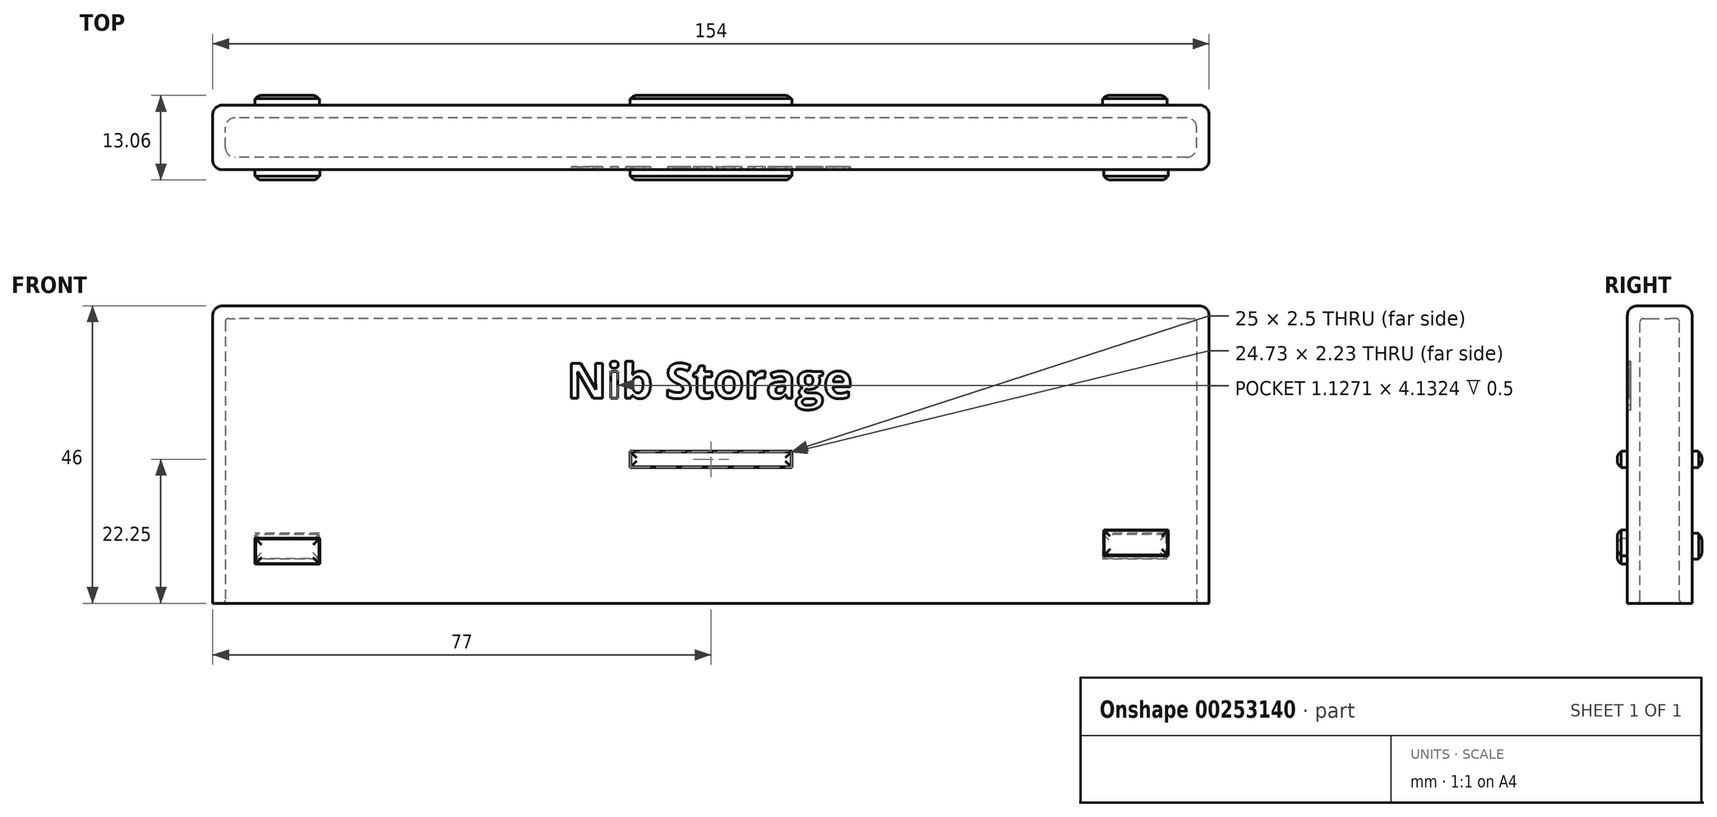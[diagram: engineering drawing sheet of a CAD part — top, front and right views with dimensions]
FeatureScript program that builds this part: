
annotation { "Feature Type Name" : "Feature", "Feature Type Description" : "" }
export const myFeature = defineFeature(function(context is Context, id is Id, definition is map)
    precondition{}
    {
        {
            var Q0;
            Q0=qCreatedBy(makeId("Top.planeOp"),FACE);
            var sketch = newSketch(context, id + "F0", { "sketchPlane" : qUnion([Q0])});
            skLineSegment(sketch, "E0.bottom", {"start": v(77, -5) * mm, "end": v(-77, -5) * mm});
            skLineSegment(sketch, "E0.top", {"start": v(77, 5) * mm, "end": v(-77, 5) * mm});
            skLineSegment(sketch, "E0.left", {"start": v(77, -5) * mm, "end": v(77, 5) * mm});
            skLineSegment(sketch, "E0.right", {"start": v(-77, -5) * mm, "end": v(-77, 5) * mm});
            skPoint(sketch, "E0.middle", {"position": v(0, 0) * mm});
            skSolve(sketch);
        }
        {
            var Q0;
            Q0 = qSketchRegion(id + "F0", true);
            extrude(context, id + "F1", {"entities" : qUnion([Q0]), "depth" : 46 * mm});
        }
        {
            var Q0;
            Q0=makeQuery(id+"F1.opExtrude","CAP_EDGE",EDGE,{"disambiguationData":[OSD([sQuery(id+"F0.wireOp",EDGE,"E0.top")])],"isStart":false});
            var Q1;
            Q1=makeQuery(id+"F1.opExtrude","CAP_EDGE",EDGE,{"disambiguationData":[OSD([sQuery(id+"F0.wireOp",EDGE,"E0.bottom")])],"isStart":false});
            var Q2;
            Q2=makeQuery(id+"F1.opExtrude","CAP_EDGE",EDGE,{"disambiguationData":[OSD([sQuery(id+"F0.wireOp",EDGE,"E0.right")])],"isStart":false});
            var Q3;
            Q3=makeQuery(id+"F1.opExtrude","CAP_EDGE",EDGE,{"disambiguationData":[OSD([sQuery(id+"F0.wireOp",EDGE,"E0.left")])],"isStart":false});
            var Q4;
            Q4=makeQuery(id+"F1.opExtrude","SWEPT_EDGE",EDGE,{"disambiguationData":[OSD([sQuery(id+"F0.wireOp",EDGE,"E0.top"),sQuery(id+"F0.wireOp",EDGE,"E0.right")])]});
            var Q5;
            Q5=makeQuery(id+"F1.opExtrude","SWEPT_EDGE",EDGE,{"disambiguationData":[OSD([sQuery(id+"F0.wireOp",EDGE,"E0.bottom"),sQuery(id+"F0.wireOp",EDGE,"E0.right")])]});
            var Q6;
            Q6=makeQuery(id+"F1.opExtrude","SWEPT_EDGE",EDGE,{"disambiguationData":[OSD([sQuery(id+"F0.wireOp",EDGE,"E0.top"),sQuery(id+"F0.wireOp",EDGE,"E0.left")])]});
            var Q7;
            Q7=makeQuery(id+"F1.opExtrude","SWEPT_EDGE",EDGE,{"disambiguationData":[OSD([sQuery(id+"F0.wireOp",EDGE,"E0.bottom"),sQuery(id+"F0.wireOp",EDGE,"E0.left")])]});
            fillet(context, id + "F2", {"entities" : qUnion([Q0, Q1, Q2, Q3, Q4, Q5, Q6, Q7]), "radius" : 1.5 * mm, "tangentPropagation" : true, "allowEdgeOverflow" : false});
        }
        {
            var Q0;
            Q0=makeQuery(id+"F1.opExtrude","CAP_FACE",FACE,{"disambiguationData":[OSD([sQuery(id+"F0.wireOp",EDGE,"E0.bottom"),sQuery(id+"F0.wireOp",EDGE,"E0.top"),sQuery(id+"F0.wireOp",EDGE,"E0.left"),sQuery(id+"F0.wireOp",EDGE,"E0.right")])],"isStart":true});
            shell(context, id + "F3", {"entities" : qUnion([Q0]), "thickness" : 1.95 * mm});
        }
        {
            var Q0;
            Q0=makeQuery(id+"F3.opShell","OFFSET_EDGE",EDGE,{"disambiguationData":[OSD([sQuery(id+"F0.wireOp",EDGE,"E0.top"),sQuery(id+"F0.wireOp",EDGE,"E0.left")])]});
            var Q1;
            Q1=makeQuery(id+"F3.opShell","OFFSET_EDGE",EDGE,{"disambiguationData":[OSD([sQuery(id+"F0.wireOp",EDGE,"E0.bottom"),sQuery(id+"F0.wireOp",EDGE,"E0.left")])]});
            var Q2;
            Q2=makeQuery(id+"F3.opShell","OFFSET_EDGE",EDGE,{"disambiguationData":[OSD([sQuery(id+"F0.wireOp",EDGE,"E0.bottom"),sQuery(id+"F0.wireOp",EDGE,"E0.right")])]});
            var Q3;
            Q3=makeQuery(id+"F3.opShell","OFFSET_EDGE",EDGE,{"disambiguationData":[OSD([sQuery(id+"F0.wireOp",EDGE,"E0.top"),sQuery(id+"F0.wireOp",EDGE,"E0.right")])]});
            fillet(context, id + "F4", {"entities" : qUnion([Q0, Q1, Q2, Q3]), "radius" : 1.5 * mm, "tangentPropagation" : true, "allowEdgeOverflow" : false});
        }
        {
            var Q0;
            Q0=makeQuery(id+"F1.opExtrude","SWEPT_FACE",FACE,{"disambiguationData":[OSD([sQuery(id+"F0.wireOp",EDGE,"E0.bottom")])]});
            var sketch = newSketch(context, id + "F5", { "sketchPlane" : qUnion([Q0])});
            skLineSegment(sketch, "E1", {"start": v(75.5, 22.25) * mm, "end": v(-75.5, 22.25) * mm, "construction": true});
            skLineSegment(sketch, "E2", {"start": v(0, 44.5) * mm, "end": v(0, 0) * mm, "construction": true});
            skLineSegment(sketch, "E3.bottom", {"start": v(-12.5, 23.5) * mm, "end": v(12.5, 23.5) * mm});
            skLineSegment(sketch, "E3.top", {"start": v(-12.5, 21) * mm, "end": v(12.5, 21) * mm});
            skLineSegment(sketch, "E3.left", {"start": v(-12.5, 23.5) * mm, "end": v(-12.5, 21) * mm});
            skLineSegment(sketch, "E3.right", {"start": v(12.5, 23.5) * mm, "end": v(12.5, 21) * mm});
            skPoint(sketch, "E3.middle", {"position": v(0, 22.25) * mm});
            skLineSegment(sketch, "E4", {"start": v(-75.5, 8.04) * mm, "end": v(75.5, 8.04) * mm, "construction": true});
            skLineSegment(sketch, "E5.bottom", {"start": v(-60.46, 6.04) * mm, "end": v(-70.46, 6.04) * mm});
            skLineSegment(sketch, "E5.top", {"start": v(-60.46, 10.04) * mm, "end": v(-70.46, 10.04) * mm});
            skLineSegment(sketch, "E5.left", {"start": v(-60.46, 6.04) * mm, "end": v(-60.46, 10.04) * mm});
            skLineSegment(sketch, "E5.right", {"start": v(-70.46, 6.04) * mm, "end": v(-70.46, 10.04) * mm});
            skPoint(sketch, "E5.middle", {"position": v(-65.46, 8.04) * mm});
            skLineSegment(sketch, "E6.bottom", {"start": v(60.69, 11.37) * mm, "end": v(70.69, 11.37) * mm});
            skLineSegment(sketch, "E6.top", {"start": v(60.69, 7.37) * mm, "end": v(70.69, 7.37) * mm});
            skLineSegment(sketch, "E6.left", {"start": v(60.69, 11.37) * mm, "end": v(60.69, 7.37) * mm});
            skLineSegment(sketch, "E6.right", {"start": v(70.69, 11.37) * mm, "end": v(70.69, 7.37) * mm});
            skPoint(sketch, "E6.middle", {"position": v(65.69, 9.37) * mm});
            skSolve(sketch);
        }
        {
            var Q0;
            Q0 = qSketchRegion(id + "F5", true);
            extrude(context, id + "F6", {"entities" : qUnion([Q0]), "operationType" : NewBodyOperationType.ADD, "depth" : 1.56 * mm});
        }
        {
            var Q0;
            Q0=makeQuery(id+"F6.opExtrude","CAP_EDGE",EDGE,{"disambiguationData":[OSD([sQuery(id+"F5.wireOp",EDGE,"E3.bottom")])],"isStart":false});
            var Q1;
            Q1=makeQuery(id+"F6.opExtrude","CAP_EDGE",EDGE,{"disambiguationData":[OSD([sQuery(id+"F5.wireOp",EDGE,"E3.right")])],"isStart":false});
            var Q2;
            Q2=makeQuery(id+"F6.opExtrude","CAP_EDGE",EDGE,{"disambiguationData":[OSD([sQuery(id+"F5.wireOp",EDGE,"E3.top")])],"isStart":false});
            var Q3;
            Q3=makeQuery(id+"F6.opExtrude","CAP_EDGE",EDGE,{"disambiguationData":[OSD([sQuery(id+"F5.wireOp",EDGE,"E3.left")])],"isStart":false});
            var Q4;
            Q4=makeQuery(id+"F6.opExtrude","CAP_EDGE",EDGE,{"disambiguationData":[OSD([sQuery(id+"F5.wireOp",EDGE,"E5.top")])],"isStart":false});
            var Q5;
            Q5=makeQuery(id+"F6.opExtrude","CAP_EDGE",EDGE,{"disambiguationData":[OSD([sQuery(id+"F5.wireOp",EDGE,"E5.left")])],"isStart":false});
            var Q6;
            Q6=makeQuery(id+"F6.opExtrude","CAP_EDGE",EDGE,{"disambiguationData":[OSD([sQuery(id+"F5.wireOp",EDGE,"E5.right")])],"isStart":false});
            var Q7;
            Q7=makeQuery(id+"F6.opExtrude","CAP_EDGE",EDGE,{"disambiguationData":[OSD([sQuery(id+"F5.wireOp",EDGE,"E6.left")])],"isStart":false});
            var Q8;
            Q8=makeQuery(id+"F6.opExtrude","CAP_EDGE",EDGE,{"disambiguationData":[OSD([sQuery(id+"F5.wireOp",EDGE,"E6.bottom")])],"isStart":false});
            var Q9;
            Q9=makeQuery(id+"F6.opExtrude","CAP_EDGE",EDGE,{"disambiguationData":[OSD([sQuery(id+"F5.wireOp",EDGE,"E6.right")])],"isStart":false});
            var Q10;
            Q10=makeQuery(id+"F6.opExtrude","CAP_EDGE",EDGE,{"disambiguationData":[OSD([sQuery(id+"F5.wireOp",EDGE,"E6.top")])],"isStart":false});
            var Q11;
            Q11=makeQuery(id+"F6.opExtrude","CAP_EDGE",EDGE,{"disambiguationData":[OSD([sQuery(id+"F5.wireOp",EDGE,"E5.bottom")])],"isStart":false});
            fillet(context, id + "F7", {"entities" : qUnion([Q0, Q1, Q2, Q3, Q4, Q5, Q6, Q7, Q8, Q9, Q10, Q11]), "radius" : 1 * mm, "tangentPropagation" : true, "allowEdgeOverflow" : false});
        }
        {
            var Q0;
            Q0=makeQuery(id+"F1.opExtrude","SWEPT_FACE",FACE,{"disambiguationData":[OSD([sQuery(id+"F0.wireOp",EDGE,"E0.top")])]});
            var sketch = newSketch(context, id + "F8", { "sketchPlane" : qUnion([Q0])});
            skLineSegment(sketch, "E7", {"start": v(-75.5, 22.25) * mm, "end": v(-71.14, 22.25) * mm, "construction": true});
            skPoint(sketch, "E7.endSnap0", {"position": v(-75.5, 22.25) * mm});
            skLineSegment(sketch, "E8", {"start": v(75.5, 22.25) * mm, "end": v(-75.5, 22.25) * mm, "construction": true});
            skLineSegment(sketch, "E9", {"start": v(0, 44.5) * mm, "end": v(0, 0) * mm, "construction": true});
            skLineSegment(sketch, "E10.bottom", {"start": v(-12.5, 23.5) * mm, "end": v(12.5, 23.5) * mm});
            skLineSegment(sketch, "E10.top", {"start": v(-12.5, 21) * mm, "end": v(12.5, 21) * mm});
            skLineSegment(sketch, "E10.left", {"start": v(-12.5, 23.5) * mm, "end": v(-12.5, 21) * mm});
            skLineSegment(sketch, "E10.right", {"start": v(12.5, 23.5) * mm, "end": v(12.5, 21) * mm});
            skPoint(sketch, "E10.middle", {"position": v(0, 22.25) * mm});
            skLineSegment(sketch, "E11", {"start": v(75.5, 8.8) * mm, "end": v(-75.5, 8.8) * mm, "construction": true});
            skLineSegment(sketch, "E12.bottom", {"start": v(60.5, 6.8) * mm, "end": v(70.5, 6.8) * mm});
            skLineSegment(sketch, "E12.top", {"start": v(60.5, 10.8) * mm, "end": v(70.5, 10.8) * mm});
            skLineSegment(sketch, "E12.left", {"start": v(60.5, 6.8) * mm, "end": v(60.5, 10.8) * mm});
            skLineSegment(sketch, "E12.right", {"start": v(70.5, 6.8) * mm, "end": v(70.5, 10.8) * mm});
            skPoint(sketch, "E12.middle", {"position": v(65.5, 8.8) * mm});
            skLineSegment(sketch, "E13.bottom", {"start": v(-70.5, 10.8) * mm, "end": v(-60.5, 10.8) * mm});
            skLineSegment(sketch, "E13.top", {"start": v(-70.5, 6.8) * mm, "end": v(-60.5, 6.8) * mm});
            skLineSegment(sketch, "E13.left", {"start": v(-70.5, 10.8) * mm, "end": v(-70.5, 6.8) * mm});
            skLineSegment(sketch, "E13.right", {"start": v(-60.5, 10.8) * mm, "end": v(-60.5, 6.8) * mm});
            skPoint(sketch, "E13.middle", {"position": v(-65.5, 8.8) * mm});
            skSolve(sketch);
        }
        {
            var Q0;
            Q0 = qSketchRegion(id + "F8", true);
            extrude(context, id + "F9", {"entities" : qUnion([Q0]), "operationType" : NewBodyOperationType.ADD, "depth" : 1.5 * mm});
        }
        {
            var Q0;
            Q0=makeQuery(id+"F9.opExtrude","CAP_EDGE",EDGE,{"disambiguationData":[OSD([sQuery(id+"F8.wireOp",EDGE,"E10.bottom")])],"isStart":false});
            var Q1;
            Q1=makeQuery(id+"F9.opExtrude","CAP_EDGE",EDGE,{"disambiguationData":[OSD([sQuery(id+"F8.wireOp",EDGE,"E10.top")])],"isStart":false});
            var Q2;
            Q2=makeQuery(id+"F9.opExtrude","CAP_EDGE",EDGE,{"disambiguationData":[OSD([sQuery(id+"F8.wireOp",EDGE,"E10.left")])],"isStart":false});
            var Q3;
            Q3=makeQuery(id+"F9.opExtrude","CAP_EDGE",EDGE,{"disambiguationData":[OSD([sQuery(id+"F8.wireOp",EDGE,"E10.right")])],"isStart":false});
            var Q4;
            Q4=makeQuery(id+"F9.opExtrude","CAP_EDGE",EDGE,{"disambiguationData":[OSD([sQuery(id+"F8.wireOp",EDGE,"E13.top")])],"isStart":false});
            var Q5;
            Q5=makeQuery(id+"F9.opExtrude","CAP_EDGE",EDGE,{"disambiguationData":[OSD([sQuery(id+"F8.wireOp",EDGE,"E13.bottom")])],"isStart":false});
            var Q6;
            Q6=makeQuery(id+"F9.opExtrude","CAP_EDGE",EDGE,{"disambiguationData":[OSD([sQuery(id+"F8.wireOp",EDGE,"E13.right")])],"isStart":false});
            var Q7;
            Q7=makeQuery(id+"F9.opExtrude","CAP_FACE",FACE,{"disambiguationData":[OSD([sQuery(id+"F8.wireOp",EDGE,"E13.bottom"),sQuery(id+"F8.wireOp",EDGE,"E13.top"),sQuery(id+"F8.wireOp",EDGE,"E13.left"),sQuery(id+"F8.wireOp",EDGE,"E13.right")])],"isStart":false});
            var Q8;
            Q8=makeQuery(id+"F9.opExtrude","CAP_EDGE",EDGE,{"disambiguationData":[OSD([sQuery(id+"F8.wireOp",EDGE,"E12.left")])],"isStart":false});
            var Q9;
            Q9=makeQuery(id+"F9.opExtrude","CAP_EDGE",EDGE,{"disambiguationData":[OSD([sQuery(id+"F8.wireOp",EDGE,"E12.right")])],"isStart":false});
            var Q10;
            Q10=makeQuery(id+"F9.opExtrude","CAP_EDGE",EDGE,{"disambiguationData":[OSD([sQuery(id+"F8.wireOp",EDGE,"E12.top")])],"isStart":false});
            var Q11;
            Q11=makeQuery(id+"F9.opExtrude","CAP_EDGE",EDGE,{"disambiguationData":[OSD([sQuery(id+"F8.wireOp",EDGE,"E12.bottom")])],"isStart":false});
            fillet(context, id + "F10", {"entities" : qUnion([Q0, Q1, Q2, Q3, Q4, Q5, Q6, Q7, Q8, Q9, Q10, Q11]), "radius" : 1 * mm, "tangentPropagation" : true, "allowEdgeOverflow" : false});
        }
        {
            var Q0;
            Q0=makeQuery(id+"F3.opShell","OFFSET_FACE",FACE,{"disambiguationData":[OSD([sQuery(id+"F0.wireOp",EDGE,"E0.left")])]});
            fillet(context, id + "F11", {"entities" : qUnion([Q0]), "radius" : .5 * mm, "tangentPropagation" : true, "allowEdgeOverflow" : false});
        }
        {
            var Q0;
            Q0 = qSketchRegion(id + "F8", true);
            extrude(context, id + "F12", {"entities" : qUnion([Q0]), "operationType" : NewBodyOperationType.ADD, "depth" : 1 * mm});
        }
        {
            var Q0;
            Q0 = qSketchRegion(id + "F5", true);
            extrude(context, id + "F13", {"entities" : qUnion([Q0]), "operationType" : NewBodyOperationType.ADD, "depth" : 1 * mm});
        }
        {
            var Q0;
            Q0=makeQuery(id+"F5.imprint","IMPRINT",FACE,{"disambiguationData":[TD([[makeQuery(id+"F5.imprint","IMPRINT",EDGE,{"derivedFrom":sQuery(id+"F5.wireOp",EDGE,"E3.bottom")}),1.0]])]});
            var sketch = newSketch(context, id + "F14", { "sketchPlane" : qUnion([Q0])});
            skText(sketch, "E14", { "text": "Nib Storage\n", "fontName": "OpenSans-Bold.ttf"});
            const initialGuessF14  = {"E14": [-0.02226, 0.03171, 1, 0, 0.00545]};
            skSetInitialGuess(sketch, initialGuessF14);
            skSolve(sketch);
        }
        {
            var Q0;
            Q0 = qSketchRegion(id + "F14", true);
            extrude(context, id + "F15", {"entities" : qUnion([Q0]), "operationType" : NewBodyOperationType.REMOVE, "oppositeDirection" : true, "depth" : .5 * mm});
        }
    });
